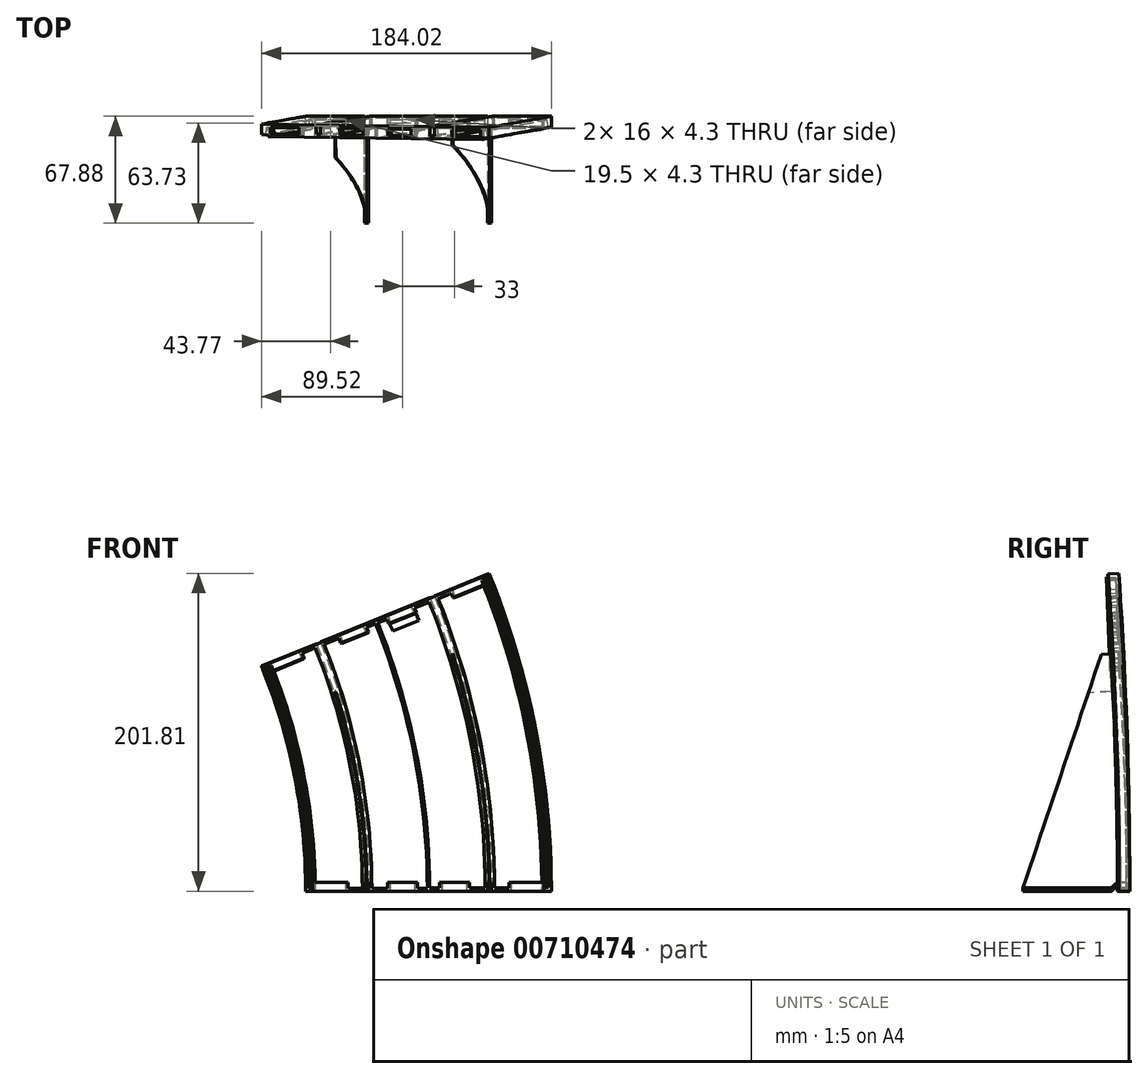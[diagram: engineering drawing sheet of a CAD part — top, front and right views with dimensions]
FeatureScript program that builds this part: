
annotation { "Feature Type Name" : "Feature", "Feature Type Description" : "" }
export const myFeature = defineFeature(function(context is Context, id is Id, definition is map)
    precondition{}
    {
        {
            var Q0;
            Q0=qCreatedBy(makeId("Top.planeOp"),FACE);
            var sketch = newSketch(context, id + "F0", { "sketchPlane" : qUnion([Q0])});
            skLineSegment(sketch, "E0", {"start": v(0, 7.8) * mm, "end": v(37.5, 7.8) * mm});
            skLineSegment(sketch, "E1", {"start": v(156, 0) * mm, "end": v(0, 0) * mm});
            skLineSegment(sketch, "E2", {"start": v(0, 0) * mm, "end": v(0, 7.8) * mm});
            skLineSegment(sketch, "E3.top", {"start": v(37.5, 1.8) * mm, "end": v(40.5, 1.8) * mm});
            skLineSegment(sketch, "E3.left", {"start": v(37.5, 7.8) * mm, "end": v(37.5, 1.8) * mm});
            skLineSegment(sketch, "E3.right", {"start": v(40.5, 7.8) * mm, "end": v(40.5, 1.8) * mm});
            skLineSegment(sketch, "E4.top", {"start": v(115.5, 1.8) * mm, "end": v(118.5, 1.8) * mm});
            skLineSegment(sketch, "E4.left", {"start": v(115.5, 7.8) * mm, "end": v(115.5, 1.8) * mm});
            skLineSegment(sketch, "E4.right", {"start": v(118.5, 7.8) * mm, "end": v(118.5, 1.8) * mm});
            skLineSegment(sketch, "E5.trimOffspring", {"start": v(40.5, 7.8) * mm, "end": v(115.5, 7.8) * mm});
            skLineSegment(sketch, "E6.trimOffspring", {"start": v(118.5, 7.8) * mm, "end": v(156, 7.8) * mm});
            skLineSegment(sketch, "E7.bottom", {"start": v(6, 5.8) * mm, "end": v(25.5, 5.8) * mm});
            skLineSegment(sketch, "E7.top", {"start": v(6, 1.5) * mm, "end": v(25.5, 1.5) * mm});
            skLineSegment(sketch, "E7.left", {"start": v(6, 5.8) * mm, "end": v(6, 1.5) * mm});
            skLineSegment(sketch, "E7.right", {"start": v(25.5, 5.8) * mm, "end": v(25.5, 1.5) * mm});
            skLineSegment(sketch, "E8.bottom", {"start": v(53.5, 5.8) * mm, "end": v(69.5, 5.8) * mm});
            skLineSegment(sketch, "E8.top", {"start": v(53.5, 1.5) * mm, "end": v(69.5, 1.5) * mm});
            skLineSegment(sketch, "E8.left", {"start": v(53.5, 5.8) * mm, "end": v(53.5, 1.5) * mm});
            skLineSegment(sketch, "E8.right", {"start": v(69.5, 5.8) * mm, "end": v(69.5, 1.5) * mm});
            skLineSegment(sketch, "E9.bottom", {"start": v(86.5, 5.8) * mm, "end": v(102.5, 5.8) * mm});
            skLineSegment(sketch, "E9.top", {"start": v(86.5, 1.5) * mm, "end": v(102.5, 1.5) * mm});
            skLineSegment(sketch, "E9.left", {"start": v(86.5, 5.8) * mm, "end": v(86.5, 1.5) * mm});
            skLineSegment(sketch, "E9.right", {"start": v(102.5, 5.8) * mm, "end": v(102.5, 1.5) * mm});
            skLineSegment(sketch, "E10.bottom", {"start": v(130.5, 5.8) * mm, "end": v(150, 5.8) * mm});
            skLineSegment(sketch, "E10.top", {"start": v(130.5, 1.5) * mm, "end": v(150, 1.5) * mm});
            skLineSegment(sketch, "E10.left", {"start": v(130.5, 5.8) * mm, "end": v(130.5, 1.5) * mm});
            skLineSegment(sketch, "E10.right", {"start": v(150, 5.8) * mm, "end": v(150, 1.5) * mm});
            skLineSegment(sketch, "E11", {"start": v(156, 7.8) * mm, "end": v(156, 0) * mm});
            skLineSegment(sketch, "E12", {"start": v(156, 0) * mm, "end": v(-362, -91.34) * mm});
            skLineSegment(sketch, "E13", {"start": v(-362, -91.34) * mm, "end": v(-356.5, -122.55) * mm});
            skSolve(sketch);
        }
        {
            var Q0;
            Q0=makeQuery(id+"F0.imprint","IMPRINT",FACE,{"disambiguationData":[TD([[makeQuery(id+"F0.imprint","IMPRINT",EDGE,{"derivedFrom":sQuery(id+"F0.wireOp",EDGE,"E0")}),-1.0]])]});
            var Q1;
            Q1=sQuery(id+"F0.wireOp",EDGE,"E13");
            revolve(context, id + "F1", {"surfaceOperationType" : NewSurfaceOperationType.NEW, "entities" : qUnion([Q0]), "axis" : qUnion([Q1]), "revolveType" : RevolveType.ONE_DIRECTION, "angle" : .25 * degree});
        }
        {
            var Q0;
            Q0=makeQuery(id+"F1.opRevolve","CAP_FACE",FACE,{"disambiguationData":[OSD([sQuery(id+"F0.wireOp",EDGE,"E0"),sQuery(id+"F0.wireOp",EDGE,"E1"),sQuery(id+"F0.wireOp",EDGE,"E2"),sQuery(id+"F0.wireOp",EDGE,"E3.top"),sQuery(id+"F0.wireOp",EDGE,"E3.left"),sQuery(id+"F0.wireOp",EDGE,"E3.right"),sQuery(id+"F0.wireOp",EDGE,"E4.top"),sQuery(id+"F0.wireOp",EDGE,"E4.left"),sQuery(id+"F0.wireOp",EDGE,"E4.right"),sQuery(id+"F0.wireOp",EDGE,"E5.trimOffspring"),sQuery(id+"F0.wireOp",EDGE,"E6.trimOffspring"),sQuery(id+"F0.wireOp",EDGE,"E7.bottom"),sQuery(id+"F0.wireOp",EDGE,"E7.top"),sQuery(id+"F0.wireOp",EDGE,"E7.left"),sQuery(id+"F0.wireOp",EDGE,"E7.right"),sQuery(id+"F0.wireOp",EDGE,"E8.bottom"),sQuery(id+"F0.wireOp",EDGE,"E8.top"),sQuery(id+"F0.wireOp",EDGE,"E8.left"),sQuery(id+"F0.wireOp",EDGE,"E8.right"),sQuery(id+"F0.wireOp",EDGE,"E9.bottom"),sQuery(id+"F0.wireOp",EDGE,"E9.top"),sQuery(id+"F0.wireOp",EDGE,"E9.left"),sQuery(id+"F0.wireOp",EDGE,"E9.right"),sQuery(id+"F0.wireOp",EDGE,"E10.bottom"),sQuery(id+"F0.wireOp",EDGE,"E10.top"),sQuery(id+"F0.wireOp",EDGE,"E10.left"),sQuery(id+"F0.wireOp",EDGE,"E10.right"),sQuery(id+"F0.wireOp",EDGE,"E11")])],"isStart":true});
            var sketch = newSketch(context, id + "F2", { "sketchPlane" : qUnion([Q0])});
            skLineSegment(sketch, "E14", {"start": v(156, -1) * mm, "end": v(154.3, -1) * mm});
            skLineSegment(sketch, "E15", {"start": v(154.3, -1) * mm, "end": v(153.3, -5.5) * mm});
            skLineSegment(sketch, "E16", {"start": v(153.3, -5.5) * mm, "end": v(151.5, -5.5) * mm});
            skLineSegment(sketch, "E17", {"start": v(151.5, -5.5) * mm, "end": v(151.5, 0) * mm});
            skLineSegment(sketch, "E18", {"start": v(151.5, 0) * mm, "end": v(150, 0) * mm});
            skLineSegment(sketch, "E19", {"start": v(150, 0) * mm, "end": v(150, -6.8) * mm});
            skLineSegment(sketch, "E20", {"start": v(150, -6.8) * mm, "end": v(120, -6.8) * mm});
            skLineSegment(sketch, "E21", {"start": v(120, -6.8) * mm, "end": v(120, 0) * mm});
            skLineSegment(sketch, "E22", {"start": v(120, 0) * mm, "end": v(114, 0) * mm});
            skLineSegment(sketch, "E23", {"start": v(114, 0) * mm, "end": v(114, -6.8) * mm});
            skLineSegment(sketch, "E24", {"start": v(114, -6.8) * mm, "end": v(78.75, -6.8) * mm});
            skLineSegment(sketch, "E25", {"start": v(42, -6.8) * mm, "end": v(42, 0) * mm});
            skLineSegment(sketch, "E26", {"start": v(42, 0) * mm, "end": v(36, 0) * mm});
            skLineSegment(sketch, "E27", {"start": v(36, 0) * mm, "end": v(36, -6.8) * mm});
            skLineSegment(sketch, "E28", {"start": v(36, -6.8) * mm, "end": v(6, -6.8) * mm});
            skLineSegment(sketch, "E29", {"start": v(6, -6.8) * mm, "end": v(6, 0) * mm});
            skLineSegment(sketch, "E30", {"start": v(6, 0) * mm, "end": v(4.5, 0) * mm});
            skLineSegment(sketch, "E31", {"start": v(4.5, 0) * mm, "end": v(4.5, -5.5) * mm});
            skLineSegment(sketch, "E32", {"start": v(4.5, -5.5) * mm, "end": v(2.7, -5.5) * mm});
            skLineSegment(sketch, "E33", {"start": v(2.7, -5.5) * mm, "end": v(1.7, -1) * mm});
            skLineSegment(sketch, "E34", {"start": v(1.7, -1) * mm, "end": v(0, -1) * mm});
            skLineSegment(sketch, "E35", {"start": v(0, -1) * mm, "end": v(0, -7.8) * mm});
            skLineSegment(sketch, "E36", {"start": v(0, -7.8) * mm, "end": v(156, -7.8) * mm});
            skLineSegment(sketch, "E37", {"start": v(156, -7.8) * mm, "end": v(156, -1) * mm});
            skLineSegment(sketch, "E38", {"start": v(77.25, 0) * mm, "end": v(77.25, -6.8) * mm});
            skLineSegment(sketch, "E39.trimOffspring", {"start": v(77.25, -6.8) * mm, "end": v(42, -6.8) * mm});
            skLineSegment(sketch, "E40", {"start": v(156, 0) * mm, "end": v(-362, 91.34) * mm});
            skLineSegment(sketch, "E41", {"start": v(-362, 91.34) * mm, "end": v(-367.9, 57.9) * mm});
            skLineSegment(sketch, "E42", {"start": v(78.75, 0) * mm, "end": v(78.75, -6.8) * mm});
            skLineSegment(sketch, "E43", {"start": v(77.25, 0) * mm, "end": v(78.75, 0) * mm});
            skSolve(sketch);
        }
        {
            var Q0;
            Q0=makeQuery(id+"F2.imprint","IMPRINT",FACE,{"disambiguationData":[TD([[makeQuery(id+"F2.imprint","IMPRINT",EDGE,{"derivedFrom":sQuery(id+"F2.wireOp",EDGE,"E14")}),1.0]])]});
            var Q1;
            Q1=sQuery(id+"F2.wireOp",EDGE,"E41");
            revolve(context, id + "F3", {"operationType" : NewBodyOperationType.ADD, "surfaceOperationType" : NewSurfaceOperationType.NEW, "entities" : qUnion([Q0]), "axis" : qUnion([Q1]), "revolveType" : RevolveType.ONE_DIRECTION, "oppositeDirection" : true, "angle" : 22.5 * degree});
        }
        {
            var Q0;
            Q0=makeQuery(id+"F1.opRevolve","CAP_FACE",FACE,{"disambiguationData":[OSD([sQuery(id+"F0.wireOp",EDGE,"E0"),sQuery(id+"F0.wireOp",EDGE,"E1"),sQuery(id+"F0.wireOp",EDGE,"E2"),sQuery(id+"F0.wireOp",EDGE,"E3.top"),sQuery(id+"F0.wireOp",EDGE,"E3.left"),sQuery(id+"F0.wireOp",EDGE,"E3.right"),sQuery(id+"F0.wireOp",EDGE,"E4.top"),sQuery(id+"F0.wireOp",EDGE,"E4.left"),sQuery(id+"F0.wireOp",EDGE,"E4.right"),sQuery(id+"F0.wireOp",EDGE,"E5.trimOffspring"),sQuery(id+"F0.wireOp",EDGE,"E6.trimOffspring"),sQuery(id+"F0.wireOp",EDGE,"E7.bottom"),sQuery(id+"F0.wireOp",EDGE,"E7.top"),sQuery(id+"F0.wireOp",EDGE,"E7.left"),sQuery(id+"F0.wireOp",EDGE,"E7.right"),sQuery(id+"F0.wireOp",EDGE,"E8.bottom"),sQuery(id+"F0.wireOp",EDGE,"E8.top"),sQuery(id+"F0.wireOp",EDGE,"E8.left"),sQuery(id+"F0.wireOp",EDGE,"E8.right"),sQuery(id+"F0.wireOp",EDGE,"E9.bottom"),sQuery(id+"F0.wireOp",EDGE,"E9.top"),sQuery(id+"F0.wireOp",EDGE,"E9.left"),sQuery(id+"F0.wireOp",EDGE,"E9.right"),sQuery(id+"F0.wireOp",EDGE,"E10.bottom"),sQuery(id+"F0.wireOp",EDGE,"E10.top"),sQuery(id+"F0.wireOp",EDGE,"E10.left"),sQuery(id+"F0.wireOp",EDGE,"E10.right"),sQuery(id+"F0.wireOp",EDGE,"E11")])],"isStart":true});
            var sketch = newSketch(context, id + "F4", { "sketchPlane" : qUnion([Q0])});
            skLineSegment(sketch, "E44.bottom", {"start": v(6, -1.5) * mm, "end": v(25.5, -1.5) * mm});
            skLineSegment(sketch, "E44.top", {"start": v(6, -5.8) * mm, "end": v(25.5, -5.8) * mm});
            skLineSegment(sketch, "E44.left", {"start": v(6, -1.5) * mm, "end": v(6, -5.8) * mm});
            skLineSegment(sketch, "E44.right", {"start": v(25.5, -1.5) * mm, "end": v(25.5, -5.8) * mm});
            skLineSegment(sketch, "E45.bottom", {"start": v(53.5, -1.5) * mm, "end": v(69.5, -1.5) * mm});
            skLineSegment(sketch, "E45.top", {"start": v(53.5, -5.8) * mm, "end": v(69.5, -5.8) * mm});
            skLineSegment(sketch, "E45.left", {"start": v(53.5, -1.5) * mm, "end": v(53.5, -5.8) * mm});
            skLineSegment(sketch, "E45.right", {"start": v(69.5, -1.5) * mm, "end": v(69.5, -5.8) * mm});
            skLineSegment(sketch, "E46.bottom", {"start": v(86.5, -1.5) * mm, "end": v(102.5, -1.5) * mm});
            skLineSegment(sketch, "E46.top", {"start": v(86.5, -5.8) * mm, "end": v(102.5, -5.8) * mm});
            skLineSegment(sketch, "E46.left", {"start": v(86.5, -1.5) * mm, "end": v(86.5, -5.8) * mm});
            skLineSegment(sketch, "E46.right", {"start": v(102.5, -1.5) * mm, "end": v(102.5, -5.8) * mm});
            skLineSegment(sketch, "E47.bottom", {"start": v(130.5, -1.5) * mm, "end": v(150, -1.5) * mm});
            skLineSegment(sketch, "E47.top", {"start": v(130.5, -5.8) * mm, "end": v(150, -5.8) * mm});
            skLineSegment(sketch, "E47.left", {"start": v(130.5, -1.5) * mm, "end": v(130.5, -5.8) * mm});
            skLineSegment(sketch, "E47.right", {"start": v(150, -1.5) * mm, "end": v(150, -5.8) * mm});
            skLineSegment(sketch, "E48.bottom", {"start": v(4.5, 0) * mm, "end": v(27, 0) * mm});
            skLineSegment(sketch, "E48.left", {"start": v(4.5, 0) * mm, "end": v(4.5, -7.3) * mm});
            skLineSegment(sketch, "E48.right", {"start": v(27, 0) * mm, "end": v(27, -7.3) * mm});
            skLineSegment(sketch, "E49.bottom", {"start": v(52, 0) * mm, "end": v(71, 0) * mm});
            skLineSegment(sketch, "E49.left", {"start": v(52, 0) * mm, "end": v(52, -7.3) * mm});
            skLineSegment(sketch, "E49.right", {"start": v(71, 0) * mm, "end": v(71, -7.3) * mm});
            skLineSegment(sketch, "E50.bottom", {"start": v(85, 0) * mm, "end": v(104, 0) * mm});
            skLineSegment(sketch, "E50.left", {"start": v(85, 0) * mm, "end": v(85, -7.3) * mm});
            skLineSegment(sketch, "E50.right", {"start": v(104, 0) * mm, "end": v(104, -7.3) * mm});
            skLineSegment(sketch, "E51.bottom", {"start": v(129, 0) * mm, "end": v(150.5, 0) * mm});
            skLineSegment(sketch, "E51.left", {"start": v(129, 0) * mm, "end": v(129, -7.3) * mm});
            skLineSegment(sketch, "E51.right", {"start": v(150.5, 0) * mm, "end": v(150.5, -7.3) * mm});
            skLineSegment(sketch, "E52", {"start": v(4.5, -7.3) * mm, "end": v(27, -7.3) * mm});
            skLineSegment(sketch, "E53", {"start": v(52, -7.3) * mm, "end": v(71, -7.3) * mm});
            skLineSegment(sketch, "E54", {"start": v(85, -7.3) * mm, "end": v(104, -7.3) * mm});
            skLineSegment(sketch, "E55", {"start": v(129, -7.3) * mm, "end": v(150.5, -7.3) * mm});
            skSolve(sketch);
        }
        {
            var Q0;
            Q0=makeQuery(id+"F4.imprint","IMPRINT",FACE,{"disambiguationData":[TD([[makeQuery(id+"F4.imprint","IMPRINT",EDGE,{"derivedFrom":sQuery(id+"F4.wireOp",EDGE,"E44.bottom")}),1.0]])]});
            var Q1;
            Q1=makeQuery(id+"F4.imprint","IMPRINT",FACE,{"disambiguationData":[TD([[makeQuery(id+"F4.imprint","IMPRINT",EDGE,{"derivedFrom":sQuery(id+"F4.wireOp",EDGE,"E45.bottom")}),1.0]])]});
            var Q2;
            Q2=makeQuery(id+"F4.imprint","IMPRINT",FACE,{"disambiguationData":[TD([[makeQuery(id+"F4.imprint","IMPRINT",EDGE,{"derivedFrom":sQuery(id+"F4.wireOp",EDGE,"E46.bottom")}),1.0]])]});
            var Q3;
            Q3=makeQuery(id+"F4.imprint","IMPRINT",FACE,{"disambiguationData":[TD([[makeQuery(id+"F4.imprint","IMPRINT",EDGE,{"derivedFrom":sQuery(id+"F4.wireOp",EDGE,"E47.bottom")}),1.0]])]});
            extrude(context, id + "F5", {"entities" : qUnion([Q0, Q1, Q2, Q3]), "operationType" : NewBodyOperationType.ADD, "oppositeDirection" : true, "depth" : 5.5 * mm, "offsetDistance" : 25 * mm});
        }
        {
            var Q0;
            Q0=makeQuery(id+"F3.opRevolve","CAP_FACE",FACE,{"disambiguationData":[OSD([sQuery(id+"F0.wireOp",EDGE,"E3.top"),sQuery(id+"F0.wireOp",EDGE,"E3.left"),sQuery(id+"F0.wireOp",EDGE,"E3.right"),sQuery(id+"F0.wireOp",EDGE,"E4.top"),sQuery(id+"F0.wireOp",EDGE,"E4.left"),sQuery(id+"F0.wireOp",EDGE,"E4.right"),sQuery(id+"F2.wireOp",EDGE,"E14"),sQuery(id+"F2.wireOp",EDGE,"E15"),sQuery(id+"F2.wireOp",EDGE,"E16"),sQuery(id+"F2.wireOp",EDGE,"E17"),sQuery(id+"F2.wireOp",EDGE,"E18"),sQuery(id+"F2.wireOp",EDGE,"E19"),sQuery(id+"F2.wireOp",EDGE,"E20"),sQuery(id+"F2.wireOp",EDGE,"E21"),sQuery(id+"F2.wireOp",EDGE,"E22"),sQuery(id+"F2.wireOp",EDGE,"E23"),sQuery(id+"F2.wireOp",EDGE,"E24"),sQuery(id+"F2.wireOp",EDGE,"E25"),sQuery(id+"F2.wireOp",EDGE,"E26"),sQuery(id+"F2.wireOp",EDGE,"E27"),sQuery(id+"F2.wireOp",EDGE,"E28"),sQuery(id+"F2.wireOp",EDGE,"E29"),sQuery(id+"F2.wireOp",EDGE,"E30"),sQuery(id+"F2.wireOp",EDGE,"E31"),sQuery(id+"F2.wireOp",EDGE,"E32"),sQuery(id+"F2.wireOp",EDGE,"E33"),sQuery(id+"F2.wireOp",EDGE,"E34"),sQuery(id+"F2.wireOp",EDGE,"E35"),sQuery(id+"F2.wireOp",EDGE,"E36"),sQuery(id+"F2.wireOp",EDGE,"E37"),sQuery(id+"F2.wireOp",EDGE,"E38"),sQuery(id+"F2.wireOp",EDGE,"E39.trimOffspring"),sQuery(id+"F2.wireOp",EDGE,"E42"),sQuery(id+"F2.wireOp",EDGE,"E43")])],"isStart":false});
            var sketch = newSketch(context, id + "F6", { "sketchPlane" : qUnion([Q0])});
            skLineSegment(sketch, "E56", {"start": v(27.73, 13.11) * mm, "end": v(65.23, 13.64) * mm});
            skLineSegment(sketch, "E57", {"start": v(65.23, 13.64) * mm, "end": v(65.31, 7.64) * mm});
            skLineSegment(sketch, "E58", {"start": v(65.31, 7.64) * mm, "end": v(68.31, 7.68) * mm});
            skLineSegment(sketch, "E59", {"start": v(68.31, 7.68) * mm, "end": v(68.23, 13.68) * mm});
            skLineSegment(sketch, "E60", {"start": v(68.23, 13.68) * mm, "end": v(143.22, 14.74) * mm});
            skLineSegment(sketch, "E61", {"start": v(143.22, 14.74) * mm, "end": v(143.3, 8.74) * mm});
            skLineSegment(sketch, "E62", {"start": v(143.3, 8.74) * mm, "end": v(146.3, 8.78) * mm});
            skLineSegment(sketch, "E63", {"start": v(146.3, 8.78) * mm, "end": v(146.22, 14.78) * mm});
            skLineSegment(sketch, "E64", {"start": v(146.22, 14.78) * mm, "end": v(183.72, 15.3) * mm});
            skLineSegment(sketch, "E65", {"start": v(183.83, 7.5) * mm, "end": v(179.33, 7.44) * mm});
            skLineSegment(sketch, "E66", {"start": v(179.33, 7.44) * mm, "end": v(32.34, 5.38) * mm});
            skLineSegment(sketch, "E67", {"start": v(32.34, 5.38) * mm, "end": v(27.84, 5.31) * mm});
            skLineSegment(sketch, "E68", {"start": v(27.84, 5.31) * mm, "end": v(27.83, 6.31) * mm});
            skLineSegment(sketch, "E69", {"start": v(27.83, 6.31) * mm, "end": v(27.73, 13.11) * mm});
            skLineSegment(sketch, "E70", {"start": v(183.72, 15.3) * mm, "end": v(183.81, 8.5) * mm});
            skLineSegment(sketch, "E71", {"start": v(183.81, 8.5) * mm, "end": v(183.83, 7.5) * mm});
            skLineSegment(sketch, "E72", {"start": v(33.9, 6.9) * mm, "end": v(53.4, 7.17) * mm});
            skLineSegment(sketch, "E73", {"start": v(53.34, 11.47) * mm, "end": v(53.4, 7.17) * mm});
            skLineSegment(sketch, "E74", {"start": v(53.34, 11.47) * mm, "end": v(33.84, 11.2) * mm});
            skLineSegment(sketch, "E75", {"start": v(33.9, 6.9) * mm, "end": v(33.84, 11.2) * mm});
            skLineSegment(sketch, "E76", {"start": v(81.34, 11.87) * mm, "end": v(97.34, 12.1) * mm});
            skLineSegment(sketch, "E77", {"start": v(97.34, 12.1) * mm, "end": v(97.4, 7.8) * mm});
            skLineSegment(sketch, "E78", {"start": v(97.4, 7.8) * mm, "end": v(81.4, 7.57) * mm});
            skLineSegment(sketch, "E79", {"start": v(81.4, 7.57) * mm, "end": v(81.34, 11.87) * mm});
            skLineSegment(sketch, "E80", {"start": v(114.27, 12.33) * mm, "end": v(130.27, 12.55) * mm});
            skLineSegment(sketch, "E81", {"start": v(130.27, 12.55) * mm, "end": v(130.33, 8.25) * mm});
            skLineSegment(sketch, "E82", {"start": v(130.33, 8.25) * mm, "end": v(114.33, 8.03) * mm});
            skLineSegment(sketch, "E83", {"start": v(114.33, 8.03) * mm, "end": v(114.27, 12.33) * mm});
            skLineSegment(sketch, "E84", {"start": v(158.27, 12.95) * mm, "end": v(177.77, 13.22) * mm});
            skLineSegment(sketch, "E85", {"start": v(177.77, 13.22) * mm, "end": v(177.83, 8.92) * mm});
            skLineSegment(sketch, "E86", {"start": v(177.83, 8.92) * mm, "end": v(158.33, 8.65) * mm});
            skLineSegment(sketch, "E87", {"start": v(158.33, 8.65) * mm, "end": v(158.27, 12.95) * mm});
            skLineSegment(sketch, "E88", {"start": v(183.83, 7.5) * mm, "end": v(-332.85, -91.1) * mm});
            skLineSegment(sketch, "E89", {"start": v(-332.85, -91.1) * mm, "end": v(-340.28, -52.18) * mm});
            skSolve(sketch);
        }
        {
            var Q0;
            Q0=makeQuery(id+"F6.imprint","IMPRINT",FACE,{"disambiguationData":[TD([[makeQuery(id+"F6.imprint","IMPRINT",EDGE,{"derivedFrom":sQuery(id+"F6.wireOp",EDGE,"E76")}),1.0]])]});
            var Q1;
            Q1=makeQuery(id+"F6.imprint","IMPRINT",FACE,{"disambiguationData":[TD([[makeQuery(id+"F6.imprint","IMPRINT",EDGE,{"derivedFrom":sQuery(id+"F6.wireOp",EDGE,"E56")}),-1.0]])]});
            var Q2;
            Q2=makeQuery(id+"F6.imprint","IMPRINT",FACE,{"disambiguationData":[TD([[makeQuery(id+"F6.imprint","IMPRINT",EDGE,{"derivedFrom":sQuery(id+"F6.wireOp",EDGE,"E72")}),-1.0]])]});
            var Q3;
            Q3=makeQuery(id+"F6.imprint","IMPRINT",FACE,{"disambiguationData":[TD([[makeQuery(id+"F6.imprint","IMPRINT",EDGE,{"derivedFrom":sQuery(id+"F6.wireOp",EDGE,"E80")}),1.0]])]});
            var Q4;
            {var subQ0=sQuery(id+"F6.wireOp",EDGE,"E87");Q4=makeQuery(id+"F6.imprint","IMPRINT",FACE,{"disambiguationData":[TD([[makeQuery(id+"F6.imprint","IMPRINT",EDGE,{"derivedFrom":subQ0}),1.0]])]});}
            var Q5;
            Q5=makeQuery(id+"F6.imprint","IMPRINT",FACE,{"disambiguationData":[TD([[makeQuery(id+"F6.imprint","IMPRINT",EDGE,{"derivedFrom":sQuery(id+"F6.wireOp",EDGE,"E67")}),-1.0]])]});
            var Q6;
            Q6=makeQuery(id+"F6.imprint","IMPRINT",FACE,{"disambiguationData":[TD([[makeQuery(id+"F6.imprint","IMPRINT",EDGE,{"derivedFrom":sQuery(id+"F6.wireOp",EDGE,"E65")}),-1.0]])]});
            var Q7;
            Q7=sQuery(id+"F6.wireOp",EDGE,"E89");
            revolve(context, id + "F7", {"operationType" : NewBodyOperationType.ADD, "surfaceOperationType" : NewSurfaceOperationType.NEW, "entities" : qUnion([Q0, Q1, Q2, Q3, Q4, Q5, Q6]), "axis" : qUnion([Q7]), "revolveType" : RevolveType.ONE_DIRECTION, "angle" : .25 * degree});
        }
        {
            var Q0;
            Q0=makeQuery(id+"F7.boolean.opBoolean","MERGE",FACE,{"derivedFrom":[makeQuery(id+"F3.opRevolve","CAP_FACE",FACE,{"disambiguationData":[OSD([sQuery(id+"F0.wireOp",EDGE,"E3.top"),sQuery(id+"F0.wireOp",EDGE,"E3.left"),sQuery(id+"F0.wireOp",EDGE,"E3.right"),sQuery(id+"F0.wireOp",EDGE,"E4.top"),sQuery(id+"F0.wireOp",EDGE,"E4.left"),sQuery(id+"F0.wireOp",EDGE,"E4.right"),sQuery(id+"F2.wireOp",EDGE,"E14"),sQuery(id+"F2.wireOp",EDGE,"E15"),sQuery(id+"F2.wireOp",EDGE,"E16"),sQuery(id+"F2.wireOp",EDGE,"E17"),sQuery(id+"F2.wireOp",EDGE,"E18"),sQuery(id+"F2.wireOp",EDGE,"E19"),sQuery(id+"F2.wireOp",EDGE,"E20"),sQuery(id+"F2.wireOp",EDGE,"E21"),sQuery(id+"F2.wireOp",EDGE,"E22"),sQuery(id+"F2.wireOp",EDGE,"E23"),sQuery(id+"F2.wireOp",EDGE,"E24"),sQuery(id+"F2.wireOp",EDGE,"E25"),sQuery(id+"F2.wireOp",EDGE,"E26"),sQuery(id+"F2.wireOp",EDGE,"E27"),sQuery(id+"F2.wireOp",EDGE,"E28"),sQuery(id+"F2.wireOp",EDGE,"E29"),sQuery(id+"F2.wireOp",EDGE,"E30"),sQuery(id+"F2.wireOp",EDGE,"E31"),sQuery(id+"F2.wireOp",EDGE,"E32"),sQuery(id+"F2.wireOp",EDGE,"E33"),sQuery(id+"F2.wireOp",EDGE,"E34"),sQuery(id+"F2.wireOp",EDGE,"E35"),sQuery(id+"F2.wireOp",EDGE,"E36"),sQuery(id+"F2.wireOp",EDGE,"E37"),sQuery(id+"F2.wireOp",EDGE,"E38"),sQuery(id+"F2.wireOp",EDGE,"E39.trimOffspring"),sQuery(id+"F2.wireOp",EDGE,"E42"),sQuery(id+"F2.wireOp",EDGE,"E43")])],"isStart":false}),makeQuery(id+"F7.opRevolve","CAP_FACE",FACE,{"disambiguationData":[OSD([sQuery(id+"F6.wireOp",EDGE,"E56"),sQuery(id+"F6.wireOp",EDGE,"E57"),sQuery(id+"F6.wireOp",EDGE,"E58"),sQuery(id+"F6.wireOp",EDGE,"E59"),sQuery(id+"F6.wireOp",EDGE,"E60"),sQuery(id+"F6.wireOp",EDGE,"E61"),sQuery(id+"F6.wireOp",EDGE,"E62"),sQuery(id+"F6.wireOp",EDGE,"E63"),sQuery(id+"F6.wireOp",EDGE,"E64"),sQuery(id+"F6.wireOp",EDGE,"E65"),sQuery(id+"F6.wireOp",EDGE,"E66"),sQuery(id+"F6.wireOp",EDGE,"E67"),sQuery(id+"F6.wireOp",EDGE,"E68"),sQuery(id+"F6.wireOp",EDGE,"E69"),sQuery(id+"F6.wireOp",EDGE,"E70"),sQuery(id+"F6.wireOp",EDGE,"E71"),sQuery(id+"F6.wireOp",EDGE,"E72"),sQuery(id+"F6.wireOp",EDGE,"E73"),sQuery(id+"F6.wireOp",EDGE,"E74"),sQuery(id+"F6.wireOp",EDGE,"E75"),sQuery(id+"F6.wireOp",EDGE,"E76"),sQuery(id+"F6.wireOp",EDGE,"E77"),sQuery(id+"F6.wireOp",EDGE,"E78"),sQuery(id+"F6.wireOp",EDGE,"E79"),sQuery(id+"F6.wireOp",EDGE,"E80"),sQuery(id+"F6.wireOp",EDGE,"E81"),sQuery(id+"F6.wireOp",EDGE,"E82"),sQuery(id+"F6.wireOp",EDGE,"E83"),sQuery(id+"F6.wireOp",EDGE,"E84"),sQuery(id+"F6.wireOp",EDGE,"E85"),sQuery(id+"F6.wireOp",EDGE,"E86"),sQuery(id+"F6.wireOp",EDGE,"E87")])],"isStart":true})]});
            var sketch = newSketch(context, id + "F8", { "sketchPlane" : qUnion([Q0])});
            skLineSegment(sketch, "E90", {"start": v(131.75, 14.07) * mm, "end": v(131.85, 6.78) * mm});
            skLineSegment(sketch, "E91", {"start": v(131.85, 6.78) * mm, "end": v(112.85, 6.5) * mm});
            skLineSegment(sketch, "E92", {"start": v(112.85, 6.5) * mm, "end": v(112.75, 13.8) * mm});
            skLineSegment(sketch, "E93", {"start": v(98.92, 6.31) * mm, "end": v(98.82, 13.61) * mm});
            skLineSegment(sketch, "E94", {"start": v(79.82, 13.35) * mm, "end": v(79.92, 6.05) * mm});
            skLineSegment(sketch, "E95", {"start": v(79.92, 6.05) * mm, "end": v(98.92, 6.31) * mm});
            skLineSegment(sketch, "E96", {"start": v(178.22, 14.73) * mm, "end": v(178.33, 7.43) * mm});
            skLineSegment(sketch, "E97", {"start": v(178.33, 7.43) * mm, "end": v(156.85, 7.13) * mm});
            skLineSegment(sketch, "E98", {"start": v(156.85, 7.13) * mm, "end": v(156.75, 14.43) * mm});
            skLineSegment(sketch, "E99", {"start": v(54.82, 13) * mm, "end": v(54.92, 5.7) * mm});
            skLineSegment(sketch, "E100", {"start": v(54.92, 5.7) * mm, "end": v(32.42, 5.38) * mm});
            skLineSegment(sketch, "E101", {"start": v(32.42, 5.38) * mm, "end": v(32.32, 12.68) * mm});
            skLineSegment(sketch, "E102", {"start": v(32.32, 12.68) * mm, "end": v(54.82, 13) * mm});
            skLineSegment(sketch, "E103", {"start": v(79.82, 13.35) * mm, "end": v(98.82, 13.61) * mm});
            skLineSegment(sketch, "E104", {"start": v(112.75, 13.8) * mm, "end": v(131.75, 14.07) * mm});
            skLineSegment(sketch, "E105", {"start": v(156.75, 14.43) * mm, "end": v(178.22, 14.73) * mm});
            skSolve(sketch);
        }
        {
            var Q0;
            Q0=makeQuery(id+"F8.imprint","IMPRINT",FACE,{"disambiguationData":[TD([[makeQuery(id+"F8.imprint","IMPRINT",EDGE,{"derivedFrom":sQuery(id+"F8.wireOp",EDGE,"E96")}),-1.0]])]});
            var Q1;
            Q1=makeQuery(id+"F8.imprint","IMPRINT",FACE,{"disambiguationData":[TD([[makeQuery(id+"F8.imprint","IMPRINT",EDGE,{"derivedFrom":sQuery(id+"F8.wireOp",EDGE,"E90")}),-1.0]])]});
            var Q2;
            Q2=makeQuery(id+"F8.imprint","IMPRINT",FACE,{"disambiguationData":[TD([[makeQuery(id+"F8.imprint","IMPRINT",EDGE,{"derivedFrom":sQuery(id+"F8.wireOp",EDGE,"E93")}),1.0]])]});
            var Q3;
            Q3=makeQuery(id+"F8.imprint","IMPRINT",FACE,{"disambiguationData":[TD([[makeQuery(id+"F8.imprint","IMPRINT",EDGE,{"derivedFrom":sQuery(id+"F8.wireOp",EDGE,"E99")}),-1.0]])]});
            extrude(context, id + "F9", {"entities" : qUnion([Q0, Q1, Q2, Q3]), "operationType" : NewBodyOperationType.ADD, "oppositeDirection" : true, "depth" : 5.5 * mm, "offsetDistance" : 25 * mm});
        }
        {
            var Q0;
            {var subQ0=sQuery(id+"F6.wireOp",EDGE,"E67");var subQ1=sQuery(id+"F6.wireOp",EDGE,"E66");var subQ2=sQuery(id+"F6.wireOp",EDGE,"E65");var subQ3=sQuery(id+"F6.wireOp",EDGE,"E69");var subQ4=sQuery(id+"F6.wireOp",EDGE,"E68");Q0=makeQuery(id+"F7.boolean.opBoolean","SPLIT",FACE,{"disambiguationData":[TD([makeQuery(id+"F1.opRevolve","SWEPT_FACE",FACE,{"disambiguationData":[OSD([sQuery(id+"F0.wireOp",EDGE,"E2")])]})])],"derivedFrom":makeQuery(id+"F7.opRevolve","CAP_FACE",FACE,{"disambiguationData":[OSD([sQuery(id+"F6.wireOp",EDGE,"E56"),sQuery(id+"F6.wireOp",EDGE,"E57"),sQuery(id+"F6.wireOp",EDGE,"E58"),sQuery(id+"F6.wireOp",EDGE,"E59"),sQuery(id+"F6.wireOp",EDGE,"E60"),sQuery(id+"F6.wireOp",EDGE,"E61"),sQuery(id+"F6.wireOp",EDGE,"E62"),sQuery(id+"F6.wireOp",EDGE,"E63"),sQuery(id+"F6.wireOp",EDGE,"E64"),subQ2,subQ1,subQ0,subQ4,subQ3,sQuery(id+"F6.wireOp",EDGE,"E70"),sQuery(id+"F6.wireOp",EDGE,"E71"),sQuery(id+"F6.wireOp",EDGE,"E72"),sQuery(id+"F6.wireOp",EDGE,"E73"),sQuery(id+"F6.wireOp",EDGE,"E74"),sQuery(id+"F6.wireOp",EDGE,"E75"),sQuery(id+"F6.wireOp",EDGE,"E76"),sQuery(id+"F6.wireOp",EDGE,"E77"),sQuery(id+"F6.wireOp",EDGE,"E78"),sQuery(id+"F6.wireOp",EDGE,"E79"),sQuery(id+"F6.wireOp",EDGE,"E80"),sQuery(id+"F6.wireOp",EDGE,"E81"),sQuery(id+"F6.wireOp",EDGE,"E82"),sQuery(id+"F6.wireOp",EDGE,"E83"),sQuery(id+"F6.wireOp",EDGE,"E84"),sQuery(id+"F6.wireOp",EDGE,"E85"),sQuery(id+"F6.wireOp",EDGE,"E86"),sQuery(id+"F6.wireOp",EDGE,"E87")])],"isStart":false})});}
            var sketch = newSketch(context, id + "F10", { "sketchPlane" : qUnion([Q0])});
            skLineSegment(sketch, "E106", {"start": v(28.92, -6.21) * mm, "end": v(24.83, -6.16) * mm});
            skLineSegment(sketch, "E107", {"start": v(24.83, -6.16) * mm, "end": v(24.83, -3.7) * mm});
            skLineSegment(sketch, "E108", {"start": v(24.83, -3.7) * mm, "end": v(31.74, -3.7) * mm});
            skLineSegment(sketch, "E109", {"start": v(31.74, -3.7) * mm, "end": v(31.7, -6.19) * mm});
            skLineSegment(sketch, "E110", {"start": v(31.7, -6.19) * mm, "end": v(28.92, -6.21) * mm});
            skSolve(sketch);
        }
        {
            var Q0;
            {var subQ3=sQuery(id+"F10.wireOp",EDGE,"E110");Q0=makeQuery(id+"F10.imprint","IMPRINT",FACE,{"disambiguationData":[TD([[makeQuery(id+"F10.imprint","IMPRINT",EDGE,{"derivedFrom":subQ3}),-1.0]])]});}
            var Q1;
            {var subQ9=sQuery(id+"F10.wireOp",EDGE,"E107");Q1=makeQuery(id+"F10.imprint","IMPRINT",FACE,{"disambiguationData":[TD([[makeQuery(id+"F10.imprint","IMPRINT",EDGE,{"derivedFrom":subQ9}),-1.0]])]});}
            extrude(context, id + "F11", {"entities" : qUnion([Q0, Q1]), "operationType" : NewBodyOperationType.REMOVE, "oppositeDirection" : true, "depth" : 25 * mm, "offsetDistance" : 25 * mm});
        }
        {
            var Q0;
            {var subQ0=sQuery(id+"F6.wireOp",EDGE,"E67");var subQ1=sQuery(id+"F6.wireOp",EDGE,"E66");var subQ2=sQuery(id+"F6.wireOp",EDGE,"E65");var subQ3=sQuery(id+"F6.wireOp",EDGE,"E71");var subQ4=sQuery(id+"F6.wireOp",EDGE,"E70");Q0=makeQuery(id+"F7.boolean.opBoolean","SPLIT",FACE,{"disambiguationData":[TD([makeQuery(id+"F1.opRevolve","SWEPT_FACE",FACE,{"disambiguationData":[OSD([sQuery(id+"F0.wireOp",EDGE,"E11")])]})])],"derivedFrom":makeQuery(id+"F7.opRevolve","CAP_FACE",FACE,{"disambiguationData":[OSD([sQuery(id+"F6.wireOp",EDGE,"E56"),sQuery(id+"F6.wireOp",EDGE,"E57"),sQuery(id+"F6.wireOp",EDGE,"E58"),sQuery(id+"F6.wireOp",EDGE,"E59"),sQuery(id+"F6.wireOp",EDGE,"E60"),sQuery(id+"F6.wireOp",EDGE,"E61"),sQuery(id+"F6.wireOp",EDGE,"E62"),sQuery(id+"F6.wireOp",EDGE,"E63"),sQuery(id+"F6.wireOp",EDGE,"E64"),subQ2,subQ1,subQ0,sQuery(id+"F6.wireOp",EDGE,"E68"),sQuery(id+"F6.wireOp",EDGE,"E69"),subQ4,subQ3,sQuery(id+"F6.wireOp",EDGE,"E72"),sQuery(id+"F6.wireOp",EDGE,"E73"),sQuery(id+"F6.wireOp",EDGE,"E74"),sQuery(id+"F6.wireOp",EDGE,"E75"),sQuery(id+"F6.wireOp",EDGE,"E76"),sQuery(id+"F6.wireOp",EDGE,"E77"),sQuery(id+"F6.wireOp",EDGE,"E78"),sQuery(id+"F6.wireOp",EDGE,"E79"),sQuery(id+"F6.wireOp",EDGE,"E80"),sQuery(id+"F6.wireOp",EDGE,"E81"),sQuery(id+"F6.wireOp",EDGE,"E82"),sQuery(id+"F6.wireOp",EDGE,"E83"),sQuery(id+"F6.wireOp",EDGE,"E84"),sQuery(id+"F6.wireOp",EDGE,"E85"),sQuery(id+"F6.wireOp",EDGE,"E86"),sQuery(id+"F6.wireOp",EDGE,"E87")])],"isStart":false})});}
            var sketch = newSketch(context, id + "F12", { "sketchPlane" : qUnion([Q0])});
            skLineSegment(sketch, "E111", {"start": v(181.5, -8.3) * mm, "end": v(185.6, -8.36) * mm});
            skLineSegment(sketch, "E112", {"start": v(185.6, -8.36) * mm, "end": v(185.6, -5.65) * mm});
            skLineSegment(sketch, "E113", {"start": v(185.6, -5.65) * mm, "end": v(178.72, -5.65) * mm});
            skLineSegment(sketch, "E114", {"start": v(178.72, -5.65) * mm, "end": v(178.69, -8.33) * mm});
            skLineSegment(sketch, "E115", {"start": v(178.69, -8.33) * mm, "end": v(181.5, -8.3) * mm});
            skSolve(sketch);
        }
        {
            var Q0;
            {var subQ1=sQuery(id+"F12.wireOp",EDGE,"E112");Q0=makeQuery(id+"F12.imprint","IMPRINT",FACE,{"disambiguationData":[TD([[makeQuery(id+"F12.imprint","IMPRINT",EDGE,{"derivedFrom":subQ1}),1.0]])]});}
            var Q1;
            {var subQ0=sQuery(id+"F6.wireOp",EDGE,"E71");var subQ1=sQuery(id+"F6.wireOp",EDGE,"E70");var subQ2=makeQuery(id+"F7.opRevolve","CAP_EDGE",EDGE,{"disambiguationData":[OSD([subQ1,subQ0])],"isStart":false});Q1=makeQuery(id+"F12.imprint","IMPRINT",FACE,{"disambiguationData":[TD([[makeQuery(id+"F12.imprint","IMPRINT",EDGE,{"derivedFrom":subQ2}),1.0]])]});}
            extrude(context, id + "F13", {"entities" : qUnion([Q0, Q1]), "operationType" : NewBodyOperationType.REMOVE, "oppositeDirection" : true, "depth" : 25 * mm, "offsetDistance" : 25 * mm});
        }
        {
            var Q0;
            Q0=qCreatedBy(makeId("Front.planeOp"),FACE);
            var sketch = newSketch(context, id + "F14", { "sketchPlane" : qUnion([Q0])});
            skLineSegment(sketch, "E116.bottom", {"start": v(-25.75, 141.73) * mm, "end": v(-22.54, 141.73) * mm});
            skLineSegment(sketch, "E116.top", {"start": v(-25.75, 142.84) * mm, "end": v(-22.54, 142.84) * mm});
            skLineSegment(sketch, "E116.left", {"start": v(-25.75, 141.73) * mm, "end": v(-25.75, 142.84) * mm});
            skLineSegment(sketch, "E116.right", {"start": v(-22.54, 141.73) * mm, "end": v(-22.54, 142.84) * mm});
            skSolve(sketch);
        }
        {
            var Q0;
            Q0=makeQuery(id+"F14.imprint","IMPRINT",FACE,{"disambiguationData":[TD([[makeQuery(id+"F14.imprint","IMPRINT",EDGE,{"derivedFrom":sQuery(id+"F14.wireOp",EDGE,"E116.bottom")}),1.0]])]});
            extrude(context, id + "F15", {"entities" : qUnion([Q0]), "operationType" : NewBodyOperationType.ADD, "depth" : 3.9 * mm, "offsetDistance" : 25 * mm});
        }
        {
            var Q0;
            Q0=qCreatedBy(makeId("Front.planeOp"),FACE);
            var sketch = newSketch(context, id + "F16", { "sketchPlane" : qUnion([Q0])});
            skLineSegment(sketch, "E117.bottom", {"start": v(113.04, 197.58) * mm, "end": v(116.3, 197.58) * mm});
            skLineSegment(sketch, "E117.top", {"start": v(113.04, 198.69) * mm, "end": v(116.3, 198.69) * mm});
            skLineSegment(sketch, "E117.left", {"start": v(113.04, 197.58) * mm, "end": v(113.04, 198.69) * mm});
            skLineSegment(sketch, "E117.right", {"start": v(116.3, 197.58) * mm, "end": v(116.3, 198.69) * mm});
            skSolve(sketch);
        }
        {
            var Q0;
            Q0=makeQuery(id+"F16.imprint","IMPRINT",FACE,{"disambiguationData":[TD([[makeQuery(id+"F16.imprint","IMPRINT",EDGE,{"derivedFrom":sQuery(id+"F16.wireOp",EDGE,"E117.bottom")}),1.0]])]});
            extrude(context, id + "F17", {"entities" : qUnion([Q0]), "depth" : 5.8 * mm, "offsetDistance" : 25 * mm});
        }
        {
            var Q0;
            {var subQ0=sQuery(id+"F0.wireOp",EDGE,"E1");var subQ1=sQuery(id+"F0.wireOp",EDGE,"E11");Q0=makeQuery(id+"F3.boolean.opBoolean","SPLIT",FACE,{"disambiguationData":[TD([makeQuery(id+"F1.opRevolve","SWEPT_FACE",FACE,{"disambiguationData":[OSD([subQ1])]})])],"derivedFrom":makeQuery(id+"F1.opRevolve","CAP_FACE",FACE,{"disambiguationData":[OSD([sQuery(id+"F0.wireOp",EDGE,"E0"),subQ0,sQuery(id+"F0.wireOp",EDGE,"E2"),sQuery(id+"F0.wireOp",EDGE,"E3.top"),sQuery(id+"F0.wireOp",EDGE,"E3.left"),sQuery(id+"F0.wireOp",EDGE,"E3.right"),sQuery(id+"F0.wireOp",EDGE,"E4.top"),sQuery(id+"F0.wireOp",EDGE,"E4.left"),sQuery(id+"F0.wireOp",EDGE,"E4.right"),sQuery(id+"F0.wireOp",EDGE,"E5.trimOffspring"),sQuery(id+"F0.wireOp",EDGE,"E6.trimOffspring"),sQuery(id+"F0.wireOp",EDGE,"E7.bottom"),sQuery(id+"F0.wireOp",EDGE,"E7.top"),sQuery(id+"F0.wireOp",EDGE,"E7.left"),sQuery(id+"F0.wireOp",EDGE,"E7.right"),sQuery(id+"F0.wireOp",EDGE,"E8.bottom"),sQuery(id+"F0.wireOp",EDGE,"E8.top"),sQuery(id+"F0.wireOp",EDGE,"E8.left"),sQuery(id+"F0.wireOp",EDGE,"E8.right"),sQuery(id+"F0.wireOp",EDGE,"E9.bottom"),sQuery(id+"F0.wireOp",EDGE,"E9.top"),sQuery(id+"F0.wireOp",EDGE,"E9.left"),sQuery(id+"F0.wireOp",EDGE,"E9.right"),sQuery(id+"F0.wireOp",EDGE,"E10.bottom"),sQuery(id+"F0.wireOp",EDGE,"E10.top"),sQuery(id+"F0.wireOp",EDGE,"E10.left"),sQuery(id+"F0.wireOp",EDGE,"E10.right"),subQ1])],"isStart":false})});}
            var sketch = newSketch(context, id + "F18", { "sketchPlane" : qUnion([Q0])});
            skLineSegment(sketch, "E118", {"start": v(154.3, 1) * mm, "end": v(157.79, 1) * mm});
            skLineSegment(sketch, "E119", {"start": v(157.79, 1) * mm, "end": v(157.79, -2.77) * mm});
            skLineSegment(sketch, "E120", {"start": v(157.79, -2.77) * mm, "end": v(151.5, -2.77) * mm});
            skLineSegment(sketch, "E121", {"start": v(151.5, -2.77) * mm, "end": v(151.5, 1) * mm});
            skLineSegment(sketch, "E122", {"start": v(151.5, 1) * mm, "end": v(154.3, 1) * mm});
            skSolve(sketch);
        }
        {
            var Q0;
            {var subQ5=sQuery(id+"F18.wireOp",EDGE,"E119");Q0=makeQuery(id+"F18.imprint","IMPRINT",FACE,{"disambiguationData":[TD([[makeQuery(id+"F18.imprint","IMPRINT",EDGE,{"derivedFrom":subQ5}),-1.0]])]});}
            var Q1;
            {var subQ2=sQuery(id+"F18.wireOp",EDGE,"E122");Q1=makeQuery(id+"F18.imprint","IMPRINT",FACE,{"disambiguationData":[TD([[makeQuery(id+"F18.imprint","IMPRINT",EDGE,{"derivedFrom":subQ2}),-1.0]])]});}
            extrude(context, id + "F19", {"entities" : qUnion([Q0, Q1]), "operationType" : NewBodyOperationType.REMOVE, "oppositeDirection" : true, "depth" : 25 * mm, "offsetDistance" : 25 * mm});
        }
        {
            var Q0;
            {var subQ0=sQuery(id+"F0.wireOp",EDGE,"E1");var subQ1=sQuery(id+"F0.wireOp",EDGE,"E2");Q0=makeQuery(id+"F3.boolean.opBoolean","SPLIT",FACE,{"disambiguationData":[TD([makeQuery(id+"F1.opRevolve","SWEPT_FACE",FACE,{"disambiguationData":[OSD([subQ1])]})])],"derivedFrom":makeQuery(id+"F1.opRevolve","CAP_FACE",FACE,{"disambiguationData":[OSD([sQuery(id+"F0.wireOp",EDGE,"E0"),subQ0,subQ1,sQuery(id+"F0.wireOp",EDGE,"E3.top"),sQuery(id+"F0.wireOp",EDGE,"E3.left"),sQuery(id+"F0.wireOp",EDGE,"E3.right"),sQuery(id+"F0.wireOp",EDGE,"E4.top"),sQuery(id+"F0.wireOp",EDGE,"E4.left"),sQuery(id+"F0.wireOp",EDGE,"E4.right"),sQuery(id+"F0.wireOp",EDGE,"E5.trimOffspring"),sQuery(id+"F0.wireOp",EDGE,"E6.trimOffspring"),sQuery(id+"F0.wireOp",EDGE,"E7.bottom"),sQuery(id+"F0.wireOp",EDGE,"E7.top"),sQuery(id+"F0.wireOp",EDGE,"E7.left"),sQuery(id+"F0.wireOp",EDGE,"E7.right"),sQuery(id+"F0.wireOp",EDGE,"E8.bottom"),sQuery(id+"F0.wireOp",EDGE,"E8.top"),sQuery(id+"F0.wireOp",EDGE,"E8.left"),sQuery(id+"F0.wireOp",EDGE,"E8.right"),sQuery(id+"F0.wireOp",EDGE,"E9.bottom"),sQuery(id+"F0.wireOp",EDGE,"E9.top"),sQuery(id+"F0.wireOp",EDGE,"E9.left"),sQuery(id+"F0.wireOp",EDGE,"E9.right"),sQuery(id+"F0.wireOp",EDGE,"E10.bottom"),sQuery(id+"F0.wireOp",EDGE,"E10.top"),sQuery(id+"F0.wireOp",EDGE,"E10.left"),sQuery(id+"F0.wireOp",EDGE,"E10.right"),sQuery(id+"F0.wireOp",EDGE,"E11")])],"isStart":false})});}
            var sketch = newSketch(context, id + "F20", { "sketchPlane" : qUnion([Q0])});
            skLineSegment(sketch, "E123", {"start": v(1.7, 1) * mm, "end": v(-2.19, 1) * mm});
            skLineSegment(sketch, "E124", {"start": v(-2.19, 1) * mm, "end": v(-2.19, -1.82) * mm});
            skLineSegment(sketch, "E125", {"start": v(-2.19, -1.82) * mm, "end": v(4.5, -1.82) * mm});
            skLineSegment(sketch, "E126", {"start": v(4.5, -1.82) * mm, "end": v(4.5, 1) * mm});
            skLineSegment(sketch, "E127", {"start": v(4.5, 1) * mm, "end": v(1.7, 1) * mm});
            skSolve(sketch);
        }
        {
            var Q0;
            {var subQ5=sQuery(id+"F20.wireOp",EDGE,"E124");Q0=makeQuery(id+"F20.imprint","IMPRINT",FACE,{"disambiguationData":[TD([[makeQuery(id+"F20.imprint","IMPRINT",EDGE,{"derivedFrom":subQ5}),1.0]])]});}
            var Q1;
            {var subQ2=sQuery(id+"F20.wireOp",EDGE,"E127");Q1=makeQuery(id+"F20.imprint","IMPRINT",FACE,{"disambiguationData":[TD([[makeQuery(id+"F20.imprint","IMPRINT",EDGE,{"derivedFrom":subQ2}),1.0]])]});}
            extrude(context, id + "F21", {"entities" : qUnion([Q0, Q1]), "operationType" : NewBodyOperationType.REMOVE, "oppositeDirection" : true, "depth" : 25 * mm, "offsetDistance" : 25 * mm});
        }
        {
            var Q0;
            Q0=qCreatedBy(makeId("Top.planeOp"),FACE);
            var sketch = newSketch(context, id + "F22", { "sketchPlane" : qUnion([Q0])});
            skLineSegment(sketch, "E128.bottom", {"start": v(38.45, 0) * mm, "end": v(38.85, 0) * mm});
            skLineSegment(sketch, "E128.top", {"start": v(38.45, -60) * mm, "end": v(38.85, -60) * mm});
            skLineSegment(sketch, "E128.left", {"start": v(38.45, 0) * mm, "end": v(38.45, -60) * mm});
            skLineSegment(sketch, "E128.right", {"start": v(38.85, 0) * mm, "end": v(38.85, -60) * mm});
            skLineSegment(sketch, "E129.bottom", {"start": v(116.49, 0) * mm, "end": v(116.89, 0) * mm});
            skLineSegment(sketch, "E129.top", {"start": v(116.49, -60) * mm, "end": v(116.89, -60) * mm});
            skLineSegment(sketch, "E129.left", {"start": v(116.49, 0) * mm, "end": v(116.49, -60) * mm});
            skLineSegment(sketch, "E129.right", {"start": v(116.89, 0) * mm, "end": v(116.89, -60) * mm});
            skLineSegment(sketch, "E130", {"start": v(0, 0) * mm, "end": v(156, 0) * mm});
            skLineSegment(sketch, "E131", {"start": v(156, 0) * mm, "end": v(-362, -91.34) * mm});
            skLineSegment(sketch, "E132", {"start": v(-362, -91.34) * mm, "end": v(-368.57, -54.14) * mm});
            skSolve(sketch);
        }
        {
            var Q0;
            {var subQ0=sQuery(id+"F22.wireOp",EDGE,"E128.top");Q0=makeQuery(id+"F22.imprint","IMPRINT",FACE,{"disambiguationData":[TD([[makeQuery(id+"F22.imprint","IMPRINT",EDGE,{"derivedFrom":subQ0}),1.0]])]});}
            var Q1;
            {var subQ0=sQuery(id+"F22.wireOp",EDGE,"E129.top");Q1=makeQuery(id+"F22.imprint","IMPRINT",FACE,{"disambiguationData":[TD([[makeQuery(id+"F22.imprint","IMPRINT",EDGE,{"derivedFrom":subQ0}),1.0]])]});}
            var Q2;
            {var subQ0=sQuery(id+"F22.wireOp",EDGE,"E130");var subQ1=sQuery(id+"F22.wireOp",EDGE,"E129.left");var subQ2=makeQuery(id+"F22.imprint","INTERSECT",VERTEX,{"derivedFrom":[subQ1,subQ0]});Q2=makeQuery(id+"F22.imprint","IMPRINT",FACE,{"disambiguationData":[TD([[makeQuery(id+"F22.imprint","IMPRINT",EDGE,{"disambiguationData":[TD([[subQ2,-1.0]])],"derivedFrom":subQ1}),1.0]])]});}
            var Q3;
            {var subQ0=sQuery(id+"F22.wireOp",EDGE,"E130");var subQ1=sQuery(id+"F22.wireOp",EDGE,"E128.left");var subQ2=makeQuery(id+"F22.imprint","INTERSECT",VERTEX,{"derivedFrom":[subQ1,subQ0]});Q3=makeQuery(id+"F22.imprint","IMPRINT",FACE,{"disambiguationData":[TD([[makeQuery(id+"F22.imprint","IMPRINT",EDGE,{"disambiguationData":[TD([[subQ2,-1.0]])],"derivedFrom":subQ1}),1.0]])]});}
            var Q4;
            Q4=sQuery(id+"F22.wireOp",EDGE,"E132");
            revolve(context, id + "F23", {"operationType" : NewBodyOperationType.ADD, "surfaceOperationType" : NewSurfaceOperationType.NEW, "entities" : qUnion([Q0, Q1, Q2, Q3]), "axis" : qUnion([Q4]), "revolveType" : RevolveType.ONE_DIRECTION, "oppositeDirection" : true, "angle" : 18 * degree});
        }
        {
            var Q0;
            Q0=qCreatedBy(makeId("Right.planeOp"),FACE);
            var sketch = newSketch(context, id + "F24", { "sketchPlane" : qUnion([Q0])});
            skLineSegment(sketch, "E133", {"start": v(-9.2, 153.76) * mm, "end": v(-62.44, -5.31) * mm});
            skLineSegment(sketch, "E134", {"start": v(-62.44, -5.31) * mm, "end": v(-5.31, -0.66) * mm});
            skLineSegment(sketch, "E135", {"start": v(-5.31, -0.66) * mm, "end": v(-0.03, 4.45) * mm});
            skLineSegment(sketch, "E136", {"start": v(-0.03, 4.45) * mm, "end": v(0, 0) * mm});
            skLineSegment(sketch, "E137", {"start": v(0, 0) * mm, "end": v(-2.8, -5.28) * mm});
            skLineSegment(sketch, "E138", {"start": v(-2.8, -5.28) * mm, "end": v(-72.1, -13.81) * mm});
            skLineSegment(sketch, "E139", {"start": v(-72.1, -13.81) * mm, "end": v(-75.54, 158.44) * mm});
            skLineSegment(sketch, "E140", {"start": v(-75.54, 158.44) * mm, "end": v(-9.2, 153.76) * mm});
            skSolve(sketch);
        }
        {
            var Q0;
            Q0=makeQuery(id+"F24.imprint","IMPRINT",FACE,{"disambiguationData":[TD([[makeQuery(id+"F24.imprint","IMPRINT",EDGE,{"derivedFrom":sQuery(id+"F24.wireOp",EDGE,"E133")}),-1.0]])]});
            extrude(context, id + "F25", {"entities" : qUnion([Q0]), "operationType" : NewBodyOperationType.REMOVE, "depth" : 163.9 * mm, "offsetDistance" : 25 * mm});
        }
        {
            var Q0;
            Q0=qCreatedBy(makeId("Top.planeOp"),FACE);
            var sketch = newSketch(context, id + "F26", { "sketchPlane" : qUnion([Q0])});
            skLineSegment(sketch, "E141.bottom", {"start": v(117.95, -4.05) * mm, "end": v(115.35, -4.05) * mm});
            skLineSegment(sketch, "E141.top", {"start": v(117.95, -60) * mm, "end": v(115.35, -60) * mm});
            skLineSegment(sketch, "E141.left", {"start": v(117.95, -4.05) * mm, "end": v(117.95, -60) * mm});
            skLineSegment(sketch, "E141.right", {"start": v(115.35, -4.05) * mm, "end": v(115.35, -60) * mm});
            skLineSegment(sketch, "E142.bottom", {"start": v(39.96, -60.08) * mm, "end": v(37.36, -60.08) * mm});
            skLineSegment(sketch, "E142.top", {"start": v(39.96, -3.96) * mm, "end": v(37.36, -3.96) * mm});
            skLineSegment(sketch, "E142.left", {"start": v(39.96, -60.08) * mm, "end": v(39.96, -3.96) * mm});
            skLineSegment(sketch, "E142.right", {"start": v(37.36, -60.08) * mm, "end": v(37.36, -3.96) * mm});
            skSolve(sketch);
        }
        {
            var Q0;
            Q0=makeQuery(id+"F26.imprint","IMPRINT",FACE,{"disambiguationData":[TD([[makeQuery(id+"F26.imprint","IMPRINT",EDGE,{"derivedFrom":sQuery(id+"F26.wireOp",EDGE,"E141.bottom")}),1.0]])]});
            var Q1;
            Q1=makeQuery(id+"F26.imprint","IMPRINT",FACE,{"disambiguationData":[TD([[makeQuery(id+"F26.imprint","IMPRINT",EDGE,{"derivedFrom":sQuery(id+"F26.wireOp",EDGE,"E142.bottom")}),-1.0]])]});
            extrude(context, id + "F27", {"entities" : qUnion([Q0, Q1]), "operationType" : NewBodyOperationType.ADD, "depth" : 2 * mm, "offsetDistance" : 25 * mm});
        }
        {
            var Q0;
            Q0=makeQuery(id+"F27.opExtrude","SWEPT_FACE",FACE,{"disambiguationData":[OSD([sQuery(id+"F26.wireOp",EDGE,"E141.left")])]});
            var sketch = newSketch(context, id + "F28", { "sketchPlane" : qUnion([Q0])});
            skLineSegment(sketch, "E143", {"start": v(-4.05, 0) * mm, "end": v(-4.05, 2) * mm});
            skLineSegment(sketch, "E144", {"start": v(-4.05, 2) * mm, "end": v(0.52, 6.17) * mm});
            skLineSegment(sketch, "E145", {"start": v(0.52, 6.17) * mm, "end": v(0.52, 4.35) * mm});
            skLineSegment(sketch, "E146", {"start": v(0.52, 4.35) * mm, "end": v(-4.05, 0) * mm});
            skSolve(sketch);
        }
        {
            var Q0;
            Q0=makeQuery(id+"F28.imprint","IMPRINT",FACE,{"disambiguationData":[TD([[makeQuery(id+"F28.imprint","IMPRINT",EDGE,{"derivedFrom":sQuery(id+"F28.wireOp",EDGE,"E143")}),1.0]])]});
            extrude(context, id + "F29", {"entities" : qUnion([Q0]), "operationType" : NewBodyOperationType.ADD, "oppositeDirection" : true, "depth" : 2.6 * mm, "offsetDistance" : 25 * mm});
        }
        {
            var Q0;
            Q0=makeQuery(id+"F27.opExtrude","SWEPT_FACE",FACE,{"disambiguationData":[OSD([sQuery(id+"F26.wireOp",EDGE,"E142.left")])]});
            var sketch = newSketch(context, id + "F30", { "sketchPlane" : qUnion([Q0])});
            skLineSegment(sketch, "E147", {"start": v(-3.96, 0) * mm, "end": v(-3.96, 2) * mm});
            skLineSegment(sketch, "E148", {"start": v(-3.96, 2) * mm, "end": v(0.53, 6.27) * mm});
            skLineSegment(sketch, "E149", {"start": v(0.53, 6.27) * mm, "end": v(0.53, 4.3) * mm});
            skLineSegment(sketch, "E150", {"start": v(0.53, 4.3) * mm, "end": v(-3.96, 0) * mm});
            skSolve(sketch);
        }
        {
            var Q0;
            Q0=makeQuery(id+"F30.imprint","IMPRINT",FACE,{"disambiguationData":[TD([[makeQuery(id+"F30.imprint","IMPRINT",EDGE,{"derivedFrom":sQuery(id+"F30.wireOp",EDGE,"E147")}),1.0]])]});
            extrude(context, id + "F31", {"entities" : qUnion([Q0]), "operationType" : NewBodyOperationType.ADD, "oppositeDirection" : true, "depth" : 2.6 * mm, "offsetDistance" : 25 * mm});
        }
        {
            var Q0;
            Q0=makeQuery(id+"F9.opExtrude","CAP_EDGE",EDGE,{"disambiguationData":[OSD([sQuery(id+"F8.wireOp",EDGE,"E100")])],"isStart":false});
            var Q1;
            Q1=makeQuery(id+"F9.opExtrude","CAP_EDGE",EDGE,{"disambiguationData":[OSD([sQuery(id+"F6.wireOp",EDGE,"E72")])],"isStart":false});
            var Q2;
            Q2=makeQuery(id+"F9.opExtrude","CAP_EDGE",EDGE,{"disambiguationData":[OSD([sQuery(id+"F6.wireOp",EDGE,"E73")])],"isStart":false});
            var Q3;
            Q3=makeQuery(id+"F9.opExtrude","CAP_EDGE",EDGE,{"disambiguationData":[OSD([sQuery(id+"F8.wireOp",EDGE,"E99")])],"isStart":false});
            var Q4;
            Q4=makeQuery(id+"F9.opExtrude","CAP_EDGE",EDGE,{"disambiguationData":[OSD([sQuery(id+"F8.wireOp",EDGE,"E94")])],"isStart":false});
            var Q5;
            Q5=makeQuery(id+"F9.opExtrude","CAP_EDGE",EDGE,{"disambiguationData":[OSD([sQuery(id+"F6.wireOp",EDGE,"E79")])],"isStart":false});
            var Q6;
            Q6=makeQuery(id+"F9.opExtrude","CAP_EDGE",EDGE,{"disambiguationData":[OSD([sQuery(id+"F8.wireOp",EDGE,"E95")])],"isStart":false});
            var Q7;
            Q7=makeQuery(id+"F9.opExtrude","CAP_EDGE",EDGE,{"disambiguationData":[OSD([sQuery(id+"F6.wireOp",EDGE,"E78")])],"isStart":false});
            var Q8;
            Q8=makeQuery(id+"F9.opExtrude","CAP_EDGE",EDGE,{"disambiguationData":[OSD([sQuery(id+"F6.wireOp",EDGE,"E77")])],"isStart":false});
            var Q9;
            Q9=makeQuery(id+"F9.opExtrude","CAP_EDGE",EDGE,{"disambiguationData":[OSD([sQuery(id+"F8.wireOp",EDGE,"E93")])],"isStart":false});
            var Q10;
            Q10=makeQuery(id+"F9.opExtrude","CAP_EDGE",EDGE,{"disambiguationData":[OSD([sQuery(id+"F8.wireOp",EDGE,"E92")])],"isStart":false});
            var Q11;
            Q11=makeQuery(id+"F9.opExtrude","CAP_EDGE",EDGE,{"disambiguationData":[OSD([sQuery(id+"F6.wireOp",EDGE,"E83")])],"isStart":false});
            var Q12;
            Q12=makeQuery(id+"F9.opExtrude","CAP_EDGE",EDGE,{"disambiguationData":[OSD([sQuery(id+"F8.wireOp",EDGE,"E91")])],"isStart":false});
            var Q13;
            Q13=makeQuery(id+"F9.opExtrude","CAP_EDGE",EDGE,{"disambiguationData":[OSD([sQuery(id+"F6.wireOp",EDGE,"E82")])],"isStart":false});
            var Q14;
            Q14=makeQuery(id+"F9.opExtrude","CAP_EDGE",EDGE,{"disambiguationData":[OSD([sQuery(id+"F6.wireOp",EDGE,"E81")])],"isStart":false});
            var Q15;
            Q15=makeQuery(id+"F9.opExtrude","CAP_EDGE",EDGE,{"disambiguationData":[OSD([sQuery(id+"F8.wireOp",EDGE,"E90")])],"isStart":false});
            var Q16;
            Q16=makeQuery(id+"F9.opExtrude","CAP_EDGE",EDGE,{"disambiguationData":[OSD([sQuery(id+"F8.wireOp",EDGE,"E98")])],"isStart":false});
            var Q17;
            Q17=makeQuery(id+"F9.opExtrude","CAP_EDGE",EDGE,{"disambiguationData":[OSD([sQuery(id+"F6.wireOp",EDGE,"E87")])],"isStart":false});
            var Q18;
            Q18=makeQuery(id+"F9.opExtrude","CAP_EDGE",EDGE,{"disambiguationData":[OSD([sQuery(id+"F8.wireOp",EDGE,"E97")])],"isStart":false});
            var Q19;
            Q19=makeQuery(id+"F9.opExtrude","CAP_EDGE",EDGE,{"disambiguationData":[OSD([sQuery(id+"F6.wireOp",EDGE,"E86")])],"isStart":false});
            var Q20;
            Q20=makeQuery(id+"F9.opExtrude","CAP_EDGE",EDGE,{"disambiguationData":[OSD([sQuery(id+"F6.wireOp",EDGE,"E76")])],"isStart":false});
            var Q21;
            Q21=makeQuery(id+"F9.opExtrude","CAP_EDGE",EDGE,{"disambiguationData":[OSD([sQuery(id+"F6.wireOp",EDGE,"E80")])],"isStart":false});
            var Q22;
            Q22=makeQuery(id+"F9.opExtrude","CAP_EDGE",EDGE,{"disambiguationData":[OSD([sQuery(id+"F6.wireOp",EDGE,"E84")])],"isStart":false});
            var Q23;
            Q23=makeQuery(id+"F9.opExtrude","CAP_EDGE",EDGE,{"disambiguationData":[OSD([sQuery(id+"F6.wireOp",EDGE,"E74")])],"isStart":false});
            chamfer(context, id + "F32", {"entities" : qUnion([Q0, Q1, Q2, Q3, Q4, Q5, Q6, Q7, Q8, Q9, Q10, Q11, Q12, Q13, Q14, Q15, Q16, Q17, Q18, Q19, Q20, Q21, Q22, Q23]), "width" : .55 * mm, "tangentPropagation" : true});
        }
        {
            var Q0;
            Q0=makeQuery(id+"F9.opExtrude","CAP_FACE",FACE,{"disambiguationData":[OSD([sQuery(id+"F6.wireOp",EDGE,"E80"),sQuery(id+"F6.wireOp",EDGE,"E81"),sQuery(id+"F6.wireOp",EDGE,"E82"),sQuery(id+"F6.wireOp",EDGE,"E83"),sQuery(id+"F8.wireOp",EDGE,"E90"),sQuery(id+"F8.wireOp",EDGE,"E91"),sQuery(id+"F8.wireOp",EDGE,"E92"),sQuery(id+"F8.wireOp",EDGE,"E104")])],"isStart":false});
            var sketch = newSketch(context, id + "F33", { "sketchPlane" : qUnion([Q0])});
            skLineSegment(sketch, "E151", {"start": v(113.71, -12.87) * mm, "end": v(130.81, -13.11) * mm});
            skLineSegment(sketch, "E152", {"start": v(130.81, -13.11) * mm, "end": v(131.21, -13.12) * mm});
            skLineSegment(sketch, "E153", {"start": v(131.21, -13.12) * mm, "end": v(131.2, -13.71) * mm});
            skLineSegment(sketch, "E154", {"start": v(113.71, -12.87) * mm, "end": v(113.31, -12.87) * mm});
            skLineSegment(sketch, "E155", {"start": v(113.31, -12.87) * mm, "end": v(113.3, -13.4) * mm});
            skLineSegment(sketch, "E156", {"start": v(113.3, -13.4) * mm, "end": v(131.2, -13.71) * mm});
            skSolve(sketch);
        }
        {
            var Q0;
            Q0=makeQuery(id+"F33.imprint","IMPRINT",FACE,{"disambiguationData":[TD([[makeQuery(id+"F33.imprint","IMPRINT",EDGE,{"derivedFrom":sQuery(id+"F33.wireOp",EDGE,"E151")}),1.0]])]});
            extrude(context, id + "F34", {"entities" : qUnion([Q0]), "operationType" : NewBodyOperationType.ADD, "depth" : 5.35 * mm, "offsetDistance" : 25 * mm});
        }
        {
            var Q0;
            Q0=makeQuery(id+"F34.opExtrude","SWEPT_FACE",FACE,{"disambiguationData":[OSD([sQuery(id+"F33.wireOp",EDGE,"E151"),sQuery(id+"F33.wireOp",EDGE,"E152"),sQuery(id+"F33.wireOp",EDGE,"E154")])]});
            var sketch = newSketch(context, id + "F35", { "sketchPlane" : qUnion([Q0])});
            skLineSegment(sketch, "E157", {"start": v(53.8, 168.88) * mm, "end": v(55.5, 164.71) * mm});
            skLineSegment(sketch, "E158", {"start": v(55.5, 164.71) * mm, "end": v(72.07, 171.46) * mm});
            skLineSegment(sketch, "E159", {"start": v(72.07, 171.46) * mm, "end": v(70.38, 175.63) * mm});
            skLineSegment(sketch, "E160", {"start": v(70.38, 175.63) * mm, "end": v(70, 175.48) * mm});
            skLineSegment(sketch, "E161", {"start": v(70, 175.48) * mm, "end": v(71.55, 171.68) * mm});
            skLineSegment(sketch, "E162", {"start": v(71.55, 171.68) * mm, "end": v(55.71, 165.23) * mm});
            skLineSegment(sketch, "E163", {"start": v(55.71, 165.23) * mm, "end": v(54.17, 169.03) * mm});
            skLineSegment(sketch, "E164", {"start": v(54.17, 169.03) * mm, "end": v(53.8, 168.88) * mm});
            skSolve(sketch);
        }
        {
            var Q0;
            Q0=makeQuery(id+"F9.opExtrude","CAP_FACE",FACE,{"disambiguationData":[OSD([sQuery(id+"F6.wireOp",EDGE,"E80"),sQuery(id+"F6.wireOp",EDGE,"E81"),sQuery(id+"F6.wireOp",EDGE,"E82"),sQuery(id+"F6.wireOp",EDGE,"E83"),sQuery(id+"F8.wireOp",EDGE,"E90"),sQuery(id+"F8.wireOp",EDGE,"E91"),sQuery(id+"F8.wireOp",EDGE,"E92"),sQuery(id+"F8.wireOp",EDGE,"E104")])],"isStart":false});
            var sketch = newSketch(context, id + "F36", { "sketchPlane" : qUnion([Q0])});
            skLineSegment(sketch, "E165", {"start": v(113.33, -11.82) * mm, "end": v(113.4, -7.07) * mm});
            skLineSegment(sketch, "E166", {"start": v(113.4, -7.07) * mm, "end": v(131.3, -7.32) * mm});
            skLineSegment(sketch, "E167", {"start": v(131.3, -7.32) * mm, "end": v(131.23, -11.82) * mm});
            skLineSegment(sketch, "E168", {"start": v(131.23, -11.82) * mm, "end": v(130.89, -11.82) * mm});
            skLineSegment(sketch, "E169", {"start": v(130.89, -11.82) * mm, "end": v(130.89, -7.71) * mm});
            skLineSegment(sketch, "E170", {"start": v(130.89, -7.71) * mm, "end": v(113.79, -7.47) * mm});
            skLineSegment(sketch, "E171", {"start": v(113.79, -7.47) * mm, "end": v(113.73, -11.82) * mm});
            skLineSegment(sketch, "E172", {"start": v(113.73, -11.82) * mm, "end": v(113.33, -11.82) * mm});
            skSolve(sketch);
        }
        {
            var Q1;
            Q1=makeQuery(id+"F35.imprint","IMPRINT",FACE,{"disambiguationData":[TD([[makeQuery(id+"F35.imprint","IMPRINT",EDGE,{"derivedFrom":sQuery(id+"F35.wireOp",EDGE,"E157")}),-1.0]])]});
            var Q2;
            Q2=makeQuery(id+"F36.imprint","IMPRINT",FACE,{"disambiguationData":[TD([[makeQuery(id+"F36.imprint","IMPRINT",EDGE,{"derivedFrom":sQuery(id+"F36.wireOp",EDGE,"E165")}),1.0]])]});
            loft(context, id + "F37", {"operationType" : NewBodyOperationType.ADD, "sheetProfilesArray" : [{ "sheetProfileEntities" : qUnion([Q1]) }, { "sheetProfileEntities" : qUnion([Q2]) }]});
        }
    });
